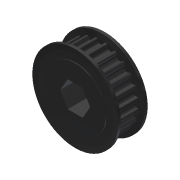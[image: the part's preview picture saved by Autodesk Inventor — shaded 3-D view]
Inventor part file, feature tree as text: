
AUTODESK INVENTOR PART (.ipt)
format: ipt  version: 2013 (Build 170138000, 138)  size: 700,928 bytes
history: native  units: in
note: dims shown in document units (in); Inventor stores cm internally (conversion verified against a paired STEP export)
features: mirror x1, other x1, imported_body x1
ambient origin geometry x8: Origin, YZ Plane, XZ Plane, XY Plane, X Axis, Y Axis, Z Axis, Center Point
feature tree (3):
  mirror  "Mirror1"
  other  "217-3227-STEP1"
  imported_body  "Base1"
